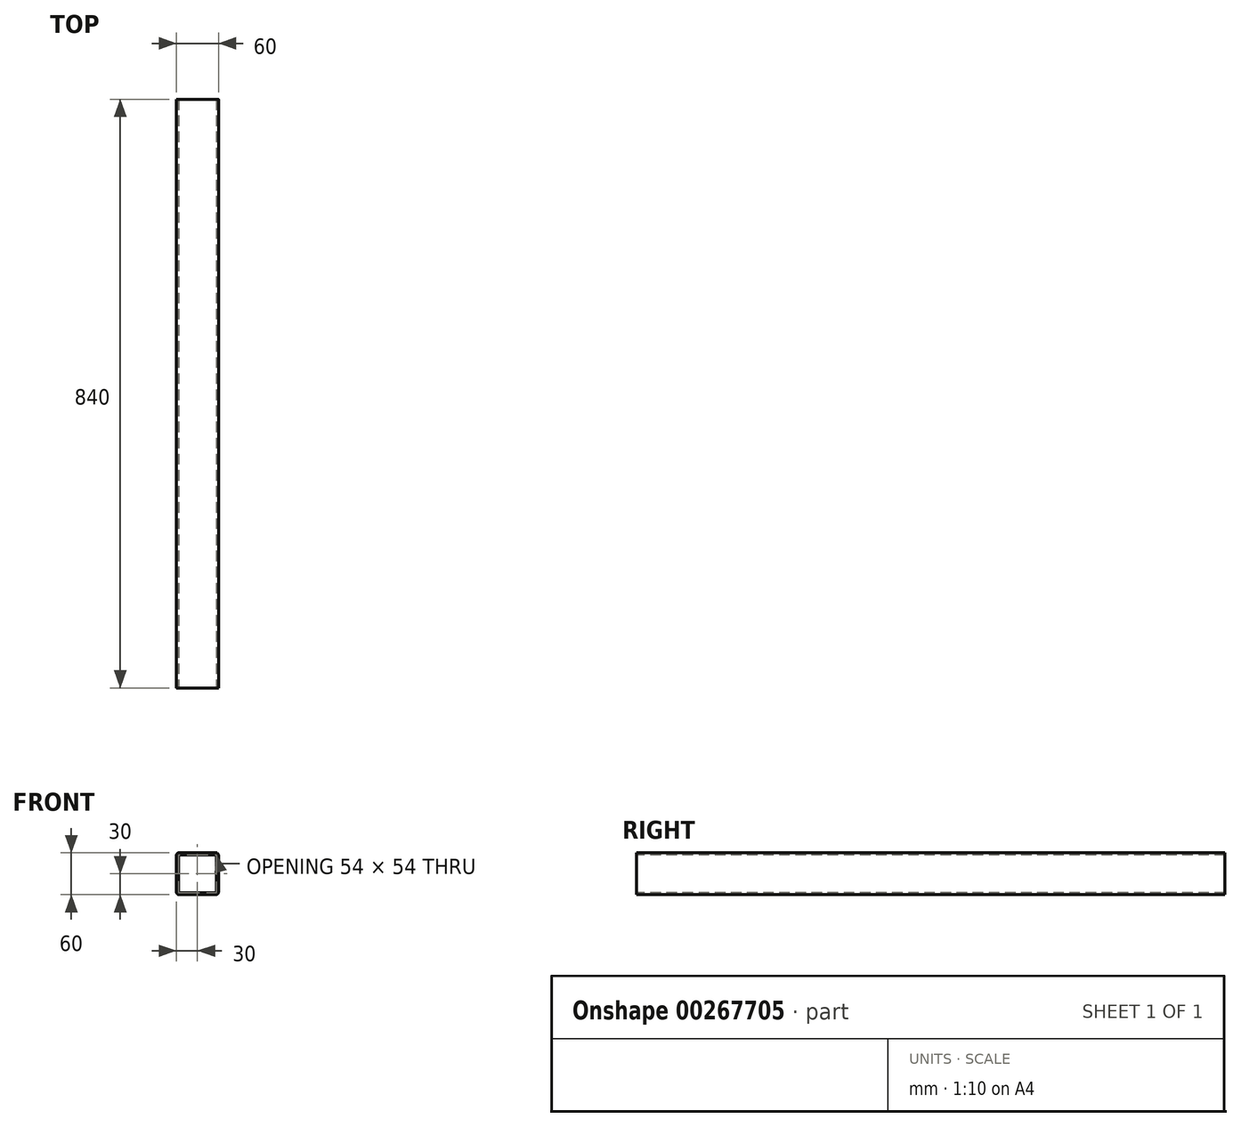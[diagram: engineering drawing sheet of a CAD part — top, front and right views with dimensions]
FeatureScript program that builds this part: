
annotation { "Feature Type Name" : "Feature", "Feature Type Description" : "" }
export const myFeature = defineFeature(function(context is Context, id is Id, definition is map)
    precondition{}
    {
        {
            var Q0;
            Q0=qCreatedBy(makeId("Front.planeOp"),FACE);
            var sketch = newSketch(context, id + "F0", { "sketchPlane" : qUnion([Q0])});
            skLineSegment(sketch, "E0.bottom", {"start": v(26, -30) * mm, "end": v(-26, -30) * mm});
            skLineSegment(sketch, "E0.top", {"start": v(26, 30) * mm, "end": v(-26, 30) * mm});
            skLineSegment(sketch, "E0.left", {"start": v(30, -26) * mm, "end": v(30, 26) * mm});
            skLineSegment(sketch, "E0.right", {"start": v(-30, -26) * mm, "end": v(-30, 26) * mm});
            skPoint(sketch, "E0.middle", {"position": v(0, 0) * mm});
            skPoint(sketch, "E1.visualSharp", {"position": v(-30, 30) * mm});
            skArc(sketch, "E1.filletArc", {"start": v(-26, 30) * mm, "mid": v(-28.83, 28.83) * mm, "end": v(-30, 26) * mm});
            skPoint(sketch, "E2.visualSharp", {"position": v(30, 30) * mm});
            skArc(sketch, "E2.filletArc", {"start": v(30, 26) * mm, "mid": v(28.83, 28.83) * mm, "end": v(26, 30) * mm});
            skPoint(sketch, "E3.visualSharp", {"position": v(30, -30) * mm});
            skArc(sketch, "E3.filletArc", {"start": v(26, -30) * mm, "mid": v(28.83, -28.83) * mm, "end": v(30, -26) * mm});
            skPoint(sketch, "E4.visualSharp", {"position": v(-30, -30) * mm});
            skArc(sketch, "E4.filletArc", {"start": v(-30, -26) * mm, "mid": v(-28.83, -28.83) * mm, "end": v(-26, -30) * mm});
            skArc(sketch, "E5.0", {"start": v(-27, -26) * mm, "mid": v(-26.7, -26.7) * mm, "end": v(-26, -27) * mm});
            skLineSegment(sketch, "E5.1", {"start": v(26, -27) * mm, "end": v(-26, -27) * mm});
            skLineSegment(sketch, "E5.2", {"start": v(-27, -26) * mm, "end": v(-27, 26) * mm});
            skArc(sketch, "E5.3", {"start": v(26, -27) * mm, "mid": v(26.7, -26.7) * mm, "end": v(27, -26) * mm});
            skArc(sketch, "E5.4", {"start": v(-26, 27) * mm, "mid": v(-26.7, 26.7) * mm, "end": v(-27, 26) * mm});
            skLineSegment(sketch, "E5.5", {"start": v(26, 27) * mm, "end": v(-26, 27) * mm});
            skArc(sketch, "E5.6", {"start": v(27, 26) * mm, "mid": v(26.7, 26.7) * mm, "end": v(26, 27) * mm});
            skLineSegment(sketch, "E5.7", {"start": v(27, -26) * mm, "end": v(27, 26) * mm});
            skSolve(sketch);
        }
        {
            var Q0;
            Q0=qSketchRegion(id+"F0",true);
            extrude(context, id + "F1", {"entities" : qUnion([Q0]), "oppositeDirection" : true, "depth" : 840 * mm});
        }
    });
